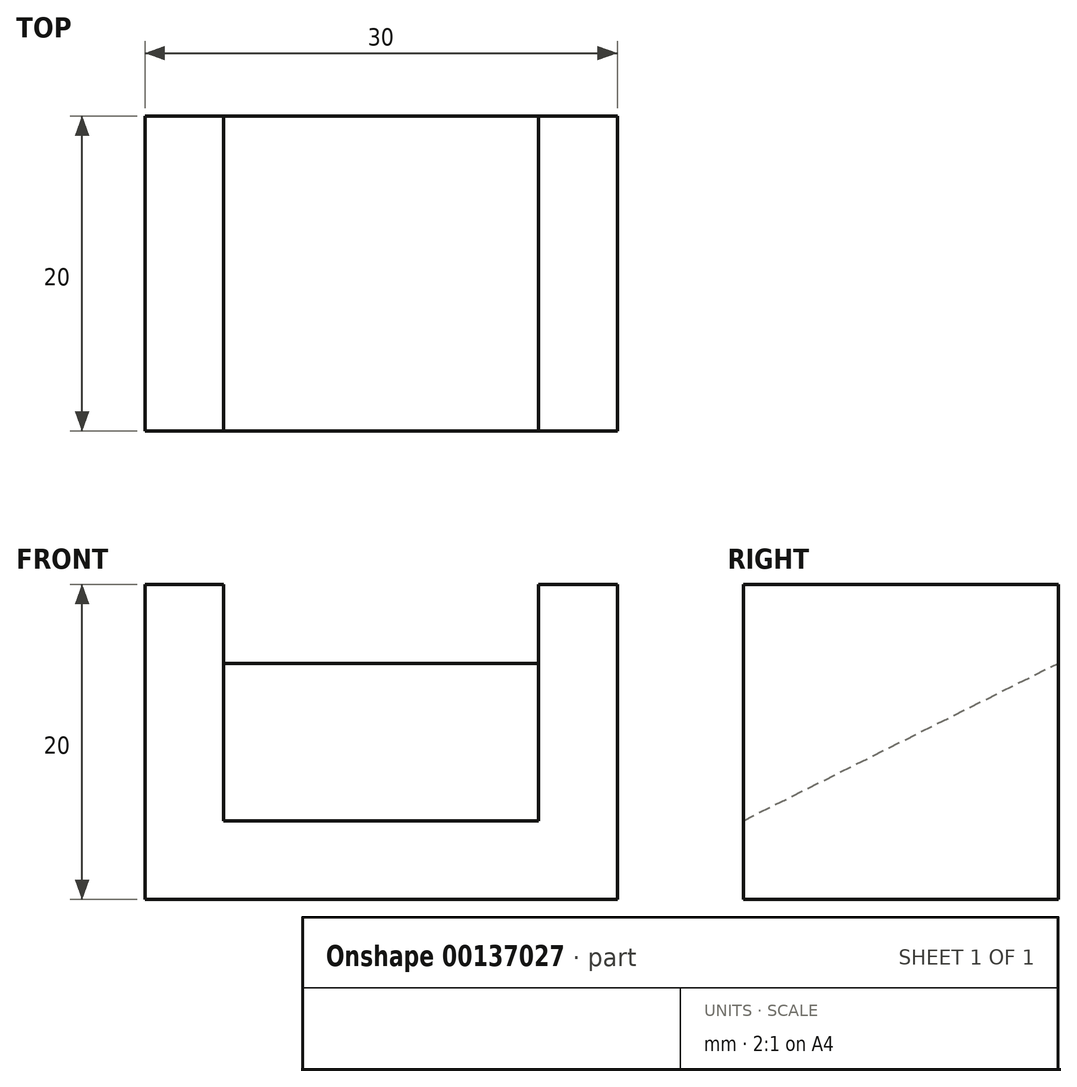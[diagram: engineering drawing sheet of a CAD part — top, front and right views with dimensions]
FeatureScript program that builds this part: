
annotation { "Feature Type Name" : "Feature", "Feature Type Description" : "" }
export const myFeature = defineFeature(function(context is Context, id is Id, definition is map)
    precondition{}
    {
        {
            var Q0;
            Q0=qCreatedBy(makeId("Front.planeOp"),FACE);
            var sketch = newSketch(context, id + "F0", { "sketchPlane" : qUnion([Q0])});
            skLineSegment(sketch, "E0.bottom", {"start": v(-15, 20) * mm, "end": v(15, 20) * mm});
            skLineSegment(sketch, "E0.top", {"start": v(-15, 0) * mm, "end": v(15, 0) * mm});
            skLineSegment(sketch, "E0.left", {"start": v(-15, 20) * mm, "end": v(-15, 0) * mm});
            skLineSegment(sketch, "E0.right", {"start": v(15, 20) * mm, "end": v(15, 0) * mm});
            skSolve(sketch);
        }
        {
            var Q0;
            Q0=makeQuery(id+"F0.imprint","IMPRINT",FACE,{"disambiguationData":[TD([[makeQuery(id+"F0.imprint","IMPRINT",EDGE,{"derivedFrom":sQuery(id+"F0.wireOp",EDGE,"E0.bottom")}),-1.0]])]});
            extrude(context, id + "F1", {"entities" : qUnion([Q0]), "oppositeDirection" : true, "depth" : 20 * mm});
        }
        {
            var Q0;
            Q0=makeQuery(id+"F1.opExtrude","SWEPT_FACE",FACE,{"disambiguationData":[OSD([sQuery(id+"F0.wireOp",EDGE,"E0.bottom")])]});
            var sketch = newSketch(context, id + "F2", { "sketchPlane" : qUnion([Q0])});
            skLineSegment(sketch, "E1.bottom", {"start": v(-10, 20) * mm, "end": v(10, 20) * mm});
            skLineSegment(sketch, "E1.top", {"start": v(-10, 0) * mm, "end": v(10, 0) * mm});
            skLineSegment(sketch, "E1.left", {"start": v(-10, 20) * mm, "end": v(-10, 0) * mm});
            skLineSegment(sketch, "E1.right", {"start": v(10, 20) * mm, "end": v(10, 0) * mm});
            skSolve(sketch);
        }
        {
            var Q0;
            Q0=makeQuery(id+"F2.imprint","IMPRINT",FACE,{"disambiguationData":[TD([[makeQuery(id+"F2.imprint","IMPRINT",EDGE,{"derivedFrom":sQuery(id+"F2.wireOp",EDGE,"E1.bottom")}),-1.0]])]});
            extrude(context, id + "F3", {"entities" : qUnion([Q0]), "operationType" : NewBodyOperationType.REMOVE, "oppositeDirection" : true, "depth" : 5 * mm});
        }
        {
            var Q0;
            Q0=makeQuery(id+"F3.boolean.opBoolean","COPY",FACE,{"derivedFrom":makeQuery(id+"F3.opExtrude","SWEPT_FACE",FACE,{"disambiguationData":[OSD([sQuery(id+"F2.wireOp",EDGE,"E1.left")])]})});
            var sketch = newSketch(context, id + "F4", { "sketchPlane" : qUnion([Q0])});
            skLineSegment(sketch, "E2.bottom", {"start": v(0, 0) * mm, "end": v(20, 0) * mm, "construction": true});
            skLineSegment(sketch, "E2.top", {"start": v(0, 20) * mm, "end": v(20, 20) * mm, "construction": true});
            skLineSegment(sketch, "E2.left", {"start": v(0, 0) * mm, "end": v(0, 20) * mm, "construction": true});
            skLineSegment(sketch, "E2.right", {"start": v(20, 0) * mm, "end": v(20, 20) * mm, "construction": true});
            skLineSegment(sketch, "E3", {"start": v(0, 5) * mm, "end": v(20, 15) * mm});
            skLineSegment(sketch, "E4", {"start": v(20, 15) * mm, "end": v(20, 20) * mm});
            skLineSegment(sketch, "E5", {"start": v(20, 20) * mm, "end": v(0, 20) * mm});
            skLineSegment(sketch, "E6", {"start": v(0, 20) * mm, "end": v(0, 5) * mm});
            skSolve(sketch);
        }
        {
            var Q0;
            Q0 = qSketchRegion(id + "F4", true);
            extrude(context, id + "F5", {"entities" : qUnion([Q0]), "operationType" : NewBodyOperationType.REMOVE, "depth" : 20 * mm});
        }
    });
